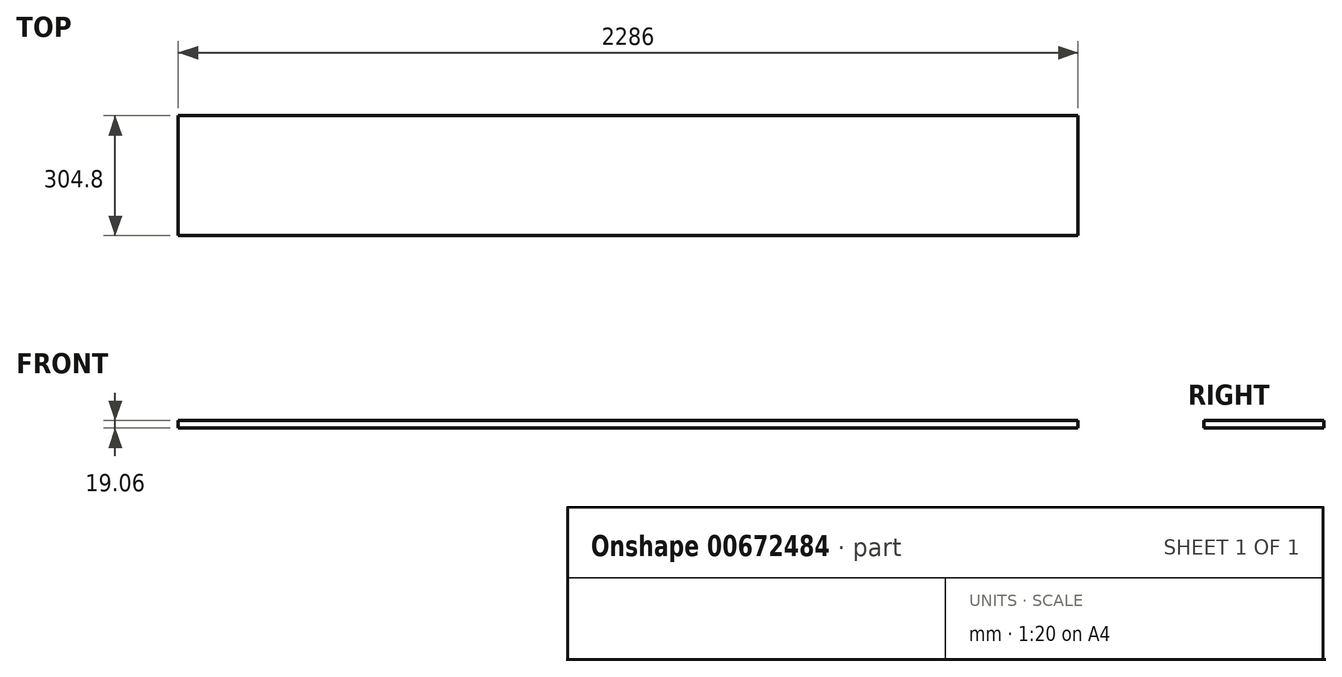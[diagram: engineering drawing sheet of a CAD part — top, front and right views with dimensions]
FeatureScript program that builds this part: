
annotation { "Feature Type Name" : "Feature", "Feature Type Description" : "" }
export const myFeature = defineFeature(function(context is Context, id is Id, definition is map)
    precondition{}
    {
        {
            var Q0;
            Q0=qCreatedBy(makeId("Top.planeOp"),FACE);
            var sketch = newSketch(context, id + "F0", { "sketchPlane" : qUnion([Q0])});
            skLineSegment(sketch, "E0.bottom", {"start": v(-1143, 152.4) * mm, "end": v(1143, 152.4) * mm});
            skLineSegment(sketch, "E0.top", {"start": v(-1143, -152.4) * mm, "end": v(1143, -152.4) * mm});
            skLineSegment(sketch, "E0.left", {"start": v(-1143, 152.4) * mm, "end": v(-1143, -152.4) * mm});
            skLineSegment(sketch, "E0.right", {"start": v(1143, 152.4) * mm, "end": v(1143, -152.4) * mm});
            skLineSegment(sketch, "E1", {"start": v(-1141.44, 190.5) * mm, "end": v(1144.56, 190.5) * mm, "construction": true});
            skPoint(sketch, "E2", {"position": v(0, 190.5) * mm});
            skSolve(sketch);
        }
        {
            var Q0;
            Q0=makeQuery(id+"F0.imprint","IMPRINT",FACE,{"disambiguationData":[TD([[makeQuery(id+"F0.imprint","IMPRINT",EDGE,{"derivedFrom":sQuery(id+"F0.wireOp",EDGE,"E0.bottom")}),-1.0]])]});
            extrude(context, id + "F1", {"entities" : qUnion([Q0]), "depth" : 9.52 * mm, "offsetDistance" : 25.4 * mm, "hasSecondDirection" : true, "secondDirectionOppositeDirection" : true, "secondDirectionDepth" : 9.52 * mm});
        }
    });
